# Revit family: Haworth_Composites_Stool_Armless
name_source: partatom
category: Furniture
revit_build: Autodesk Revit 2018 (Build: 20170223_1515(x64)
units: mm (PartAtom-declared; Revit-internal decimal feet)

## family parameters
Always vertical = Yes
Cut with Voids When Loaded = No
OmniClass Number = 23.40.70.14.64.11
OmniClass Title = Office Furniture
Room Calculation Point = No
Shared = No
Work Plane-Based = No

## types (2) — shared parameters
Actual Depth = 22"
Actual Height = 41 1/8"
Actual Width = 22 3/8"
Assembly Code = E2020200
Glide Finish = Haworth _ Polymer _ Black
Manufacturer = Haworth
Model = Haworth Composites Stool
Revision Number = 1
Size = Verify Final Dim. w/ Haworth
Sustainability Info = http://www.haworth.com
URL = https://www.haworth.com
URL - Product = https://www.haworth.com
Warranty = http://www.haworth.com

## per-type parameters (varying)
| type | Description | Slat Back | Upholstered Back |
| 4049-00 - Upholstered Back | Haworth Composites Stool - Armless - Upholstered Back | No | Yes |
| 4249-00 - Slat Back | Haworth Composites Stool - Armless - Slat Back | Yes | No |

## geometry (parser evidence)
native form markers: Sweep x1
no freeform markers — native parametric forms only
